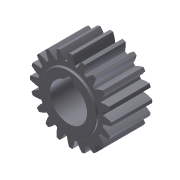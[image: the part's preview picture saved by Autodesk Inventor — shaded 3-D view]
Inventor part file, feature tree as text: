
AUTODESK INVENTOR PART (.ipt)
format: ipt  version: 2011 (Build 150239000, 239)  size: 240,640 bytes
history: native  units: mm (DEFAULTED — no unit token found)
features: other x4, sketch x4, extrude x3, plane x3, fillet x1
ambient origin geometry x8: Origin, YZ Plane, XZ Plane, XY Plane, X Axis, Y Axis, Z Axis, Center Point
bodies: Solid1 (feature_tree)
feature tree (15):
  other  "Gear 20T 20dp 500key"
  extrude  "Extrusion1"  Depth=13.97mm TaperAngle=0.0deg
  plane  "Work Plane1"
  plane  "Work Plane2"
  plane  "Work Plane3"
  other  "Spur Gear"
  extrude  "Extrusion2"  Depth=76.2mm TaperAngle=0.0deg
  extrude  "Extrusion3"  TaperAngle=0.0deg  [1 undecoded]
  fillet  "Fillet1"  Radius=63.5mm
  sketch  "Sketch1"  dims[d0=27.94mm d1=13.97mm d2=0.0mm]
  sketch  "Sketch2"  dims[d3=25.4mm d4=76.2mm d5=0.0mm]
  other  "Srf1"
  sketch  "Sketch3"  dims[d6=0.0mm d7=1.570796mm d9=0.0mm d14=0.0mm d15=63.5mm]
  sketch  "Sketch4"  dims[d16=0.0mm d17=0.0mm d18=0.0mm d19=63.5mm d20=19.05mm d21=0.762mm d22=0.0mm d23=12.7mm d24=3.175mm d25=3.175mm d26=0.762mm d27=0.0mm d28=0.254mm]
  other  "Pitch Diameter"
note: 1 required parameter value undecoded (feature->parameter linkage not recoverable at this tier; creation-order binding heuristic only, values carry confidence <= 0.55)
